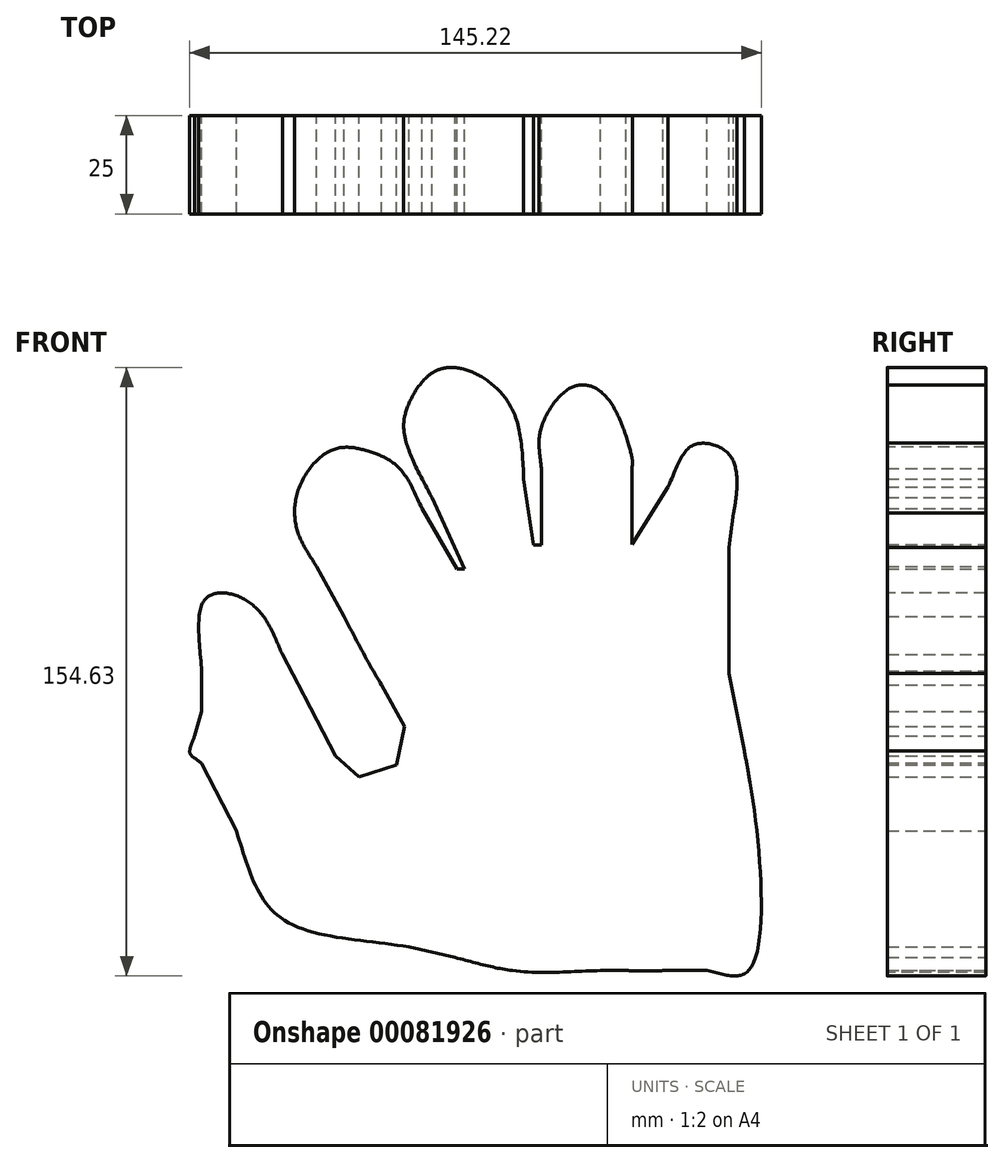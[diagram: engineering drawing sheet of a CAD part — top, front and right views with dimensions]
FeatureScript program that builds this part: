
annotation { "Feature Type Name" : "Feature", "Feature Type Description" : "" }
export const myFeature = defineFeature(function(context is Context, id is Id, definition is map)
    precondition{}
    {
        {
            var Q0;
            Q0=qCreatedBy(makeId("Front.planeOp"),FACE);
            var sketch = newSketch(context, id + "F0", { "sketchPlane" : qUnion([Q0])});
            skLineSegment(sketch, "E0", {"start": v(-6.6, -64.84) * mm, "end": v(53.4, -64.84) * mm});
            skLineSegment(sketch, "E1", {"start": v(53.4, -64.84) * mm, "end": v(53.4, -14.84) * mm});
            skLineSegment(sketch, "E2", {"start": v(53.4, -14.84) * mm, "end": v(48.4, 10.68) * mm});
            skLineSegment(sketch, "E3", {"start": v(48.4, 10.68) * mm, "end": v(48.4, 42.68) * mm});
            skLineSegment(sketch, "E4", {"start": v(48.4, 42.68) * mm, "end": v(50.4, 57.54) * mm});
            skLineSegment(sketch, "E5", {"start": v(50.4, 57.54) * mm, "end": v(48.4, 66.32) * mm});
            skLineSegment(sketch, "E6", {"start": v(48.4, 66.32) * mm, "end": v(39.76, 68.82) * mm});
            skLineSegment(sketch, "E7", {"start": v(39.76, 68.82) * mm, "end": v(23.76, 43.44) * mm});
            skLineSegment(sketch, "E8", {"start": v(23.76, 43.44) * mm, "end": v(23.76, 65.44) * mm});
            skLineSegment(sketch, "E9", {"start": v(23.76, 65.44) * mm, "end": v(20.76, 74.98) * mm});
            skLineSegment(sketch, "E10", {"start": v(20.76, 74.98) * mm, "end": v(14.76, 82.98) * mm});
            skLineSegment(sketch, "E11", {"start": v(14.76, 82.98) * mm, "end": v(7.76, 82.98) * mm});
            skLineSegment(sketch, "E12", {"start": v(7.76, 82.98) * mm, "end": v(0.76, 73.23) * mm});
            skLineSegment(sketch, "E13", {"start": v(0.76, 73.23) * mm, "end": v(0.76, 43.23) * mm});
            skLineSegment(sketch, "E14", {"start": v(0.76, 43.23) * mm, "end": v(-1.24, 43.23) * mm});
            skLineSegment(sketch, "E15", {"start": v(-1.24, 43.23) * mm, "end": v(-6.24, 76.86) * mm});
            skLineSegment(sketch, "E16", {"start": v(-6.24, 76.86) * mm, "end": v(-13.74, 85.58) * mm});
            skLineSegment(sketch, "E17", {"start": v(-28.74, 85.58) * mm, "end": v(-33.74, 76.92) * mm});
            skLineSegment(sketch, "E18", {"start": v(-33.74, 76.92) * mm, "end": v(-33.74, 69.92) * mm});
            skLineSegment(sketch, "E19", {"start": v(-33.74, 69.92) * mm, "end": v(-18.74, 37.2) * mm});
            skLineSegment(sketch, "E20", {"start": v(-18.74, 37.2) * mm, "end": v(-20.74, 37.2) * mm});
            skLineSegment(sketch, "E21", {"start": v(-20.74, 37.2) * mm, "end": v(-35.74, 63.17) * mm});
            skLineSegment(sketch, "E22", {"start": v(-35.74, 63.17) * mm, "end": v(-43.74, 67.3) * mm});
            skLineSegment(sketch, "E23", {"start": v(-43.74, 67.3) * mm, "end": v(-52.74, 67.3) * mm});
            skLineSegment(sketch, "E24", {"start": v(-52.74, 67.3) * mm, "end": v(-61.02, 57.28) * mm});
            skLineSegment(sketch, "E25", {"start": v(-61.02, 57.28) * mm, "end": v(-61.02, 46.28) * mm});
            skLineSegment(sketch, "E26", {"start": v(-61.02, 46.28) * mm, "end": v(-34.02, -2.78) * mm});
            skLineSegment(sketch, "E27", {"start": v(-34.02, -2.78) * mm, "end": v(-36.02, -12.58) * mm});
            skLineSegment(sketch, "E28", {"start": v(-36.02, -12.58) * mm, "end": v(-45.56, -15.58) * mm});
            skLineSegment(sketch, "E29", {"start": v(-45.56, -15.58) * mm, "end": v(-51.56, -10.29) * mm});
            skLineSegment(sketch, "E30", {"start": v(-51.56, -10.29) * mm, "end": v(-70.56, 26.04) * mm});
            skLineSegment(sketch, "E31", {"start": v(-70.56, 26.04) * mm, "end": v(-79.22, 31.04) * mm});
            skLineSegment(sketch, "E32", {"start": v(-79.22, 31.04) * mm, "end": v(-79.22, 28.04) * mm});
            skLineSegment(sketch, "E33", {"start": v(-79.22, 31.04) * mm, "end": v(-85.55, 28.04) * mm});
            skLineSegment(sketch, "E34", {"start": v(-85.55, 28.04) * mm, "end": v(-85.55, 1.04) * mm});
            skLineSegment(sketch, "E35", {"start": v(-85.55, 1.04) * mm, "end": v(-88.55, -9.54) * mm});
            skLineSegment(sketch, "E36", {"start": v(-88.55, -9.54) * mm, "end": v(-85.55, -12.19) * mm});
            skLineSegment(sketch, "E37", {"start": v(-85.55, -12.19) * mm, "end": v(-65.55, -51.38) * mm});
            skLineSegment(sketch, "E38", {"start": v(-65.55, -51.38) * mm, "end": v(-6.6, -64.84) * mm});
            skLineSegment(sketch, "E39", {"start": v(-65.55, -51.38) * mm, "end": v(-44.93, -34.8) * mm});
            skLineSegment(sketch, "E40", {"start": v(-44.93, -34.8) * mm, "end": v(-5.2, -48.3) * mm});
            skLineSegment(sketch, "E41", {"start": v(-5.2, -48.3) * mm, "end": v(-6.6, -64.84) * mm});
            skLineSegment(sketch, "E42", {"start": v(-5.2, -48.3) * mm, "end": v(15.79, -48.3) * mm});
            skLineSegment(sketch, "E43", {"start": v(15.79, -48.3) * mm, "end": v(15.79, -64.84) * mm});
            skLineSegment(sketch, "E44", {"start": v(15.79, -64.84) * mm, "end": v(15.79, -48.3) * mm});
            skLineSegment(sketch, "E45", {"start": v(15.79, -48.3) * mm, "end": v(31.68, -48.3) * mm});
            skLineSegment(sketch, "E46", {"start": v(31.68, -48.3) * mm, "end": v(31.68, -64.84) * mm});
            skLineSegment(sketch, "E47", {"start": v(31.68, -64.84) * mm, "end": v(31.68, -48.3) * mm});
            skLineSegment(sketch, "E48", {"start": v(31.68, -48.3) * mm, "end": v(42.8, -48.3) * mm});
            skLineSegment(sketch, "E49", {"start": v(42.8, -48.3) * mm, "end": v(42.8, -64.84) * mm});
            skLineSegment(sketch, "E50", {"start": v(42.8, -64.84) * mm, "end": v(42.8, -48.3) * mm});
            skLineSegment(sketch, "E51", {"start": v(42.8, -48.3) * mm, "end": v(37.56, -15.08) * mm});
            skLineSegment(sketch, "E52", {"start": v(37.56, -15.08) * mm, "end": v(53.4, -14.84) * mm});
            skLineSegment(sketch, "E53", {"start": v(31.68, -48.3) * mm, "end": v(24.85, -15.88) * mm});
            skLineSegment(sketch, "E54", {"start": v(24.85, -15.88) * mm, "end": v(37.56, -15.08) * mm});
            skLineSegment(sketch, "E55", {"start": v(15.79, -48.3) * mm, "end": v(10.07, -16.51) * mm});
            skLineSegment(sketch, "E56", {"start": v(10.07, -16.51) * mm, "end": v(24.85, -15.88) * mm});
            skLineSegment(sketch, "E57", {"start": v(-5.2, -48.3) * mm, "end": v(-8.7, -16.04) * mm});
            skLineSegment(sketch, "E58", {"start": v(-8.7, -16.04) * mm, "end": v(10.07, -16.51) * mm});
            skLineSegment(sketch, "E59", {"start": v(-36.02, -12.58) * mm, "end": v(-8.7, -16.04) * mm});
            skLineSegment(sketch, "E60", {"start": v(-45.56, -15.58) * mm, "end": v(-44.93, -34.8) * mm});
            skLineSegment(sketch, "E61", {"start": v(-26.95, -40.9) * mm, "end": v(-22.36, -14.3) * mm});
            skLineSegment(sketch, "E62", {"start": v(-22.36, -14.3) * mm, "end": v(-26.95, -40.9) * mm});
            skLineSegment(sketch, "E63", {"start": v(-26.95, -40.9) * mm, "end": v(-32.9, -58.83) * mm});
            skLineSegment(sketch, "E64", {"start": v(-32.9, -58.83) * mm, "end": v(-26.95, -40.9) * mm});
            skLineSegment(sketch, "E65", {"start": v(-76.76, -29.41) * mm, "end": v(-62.41, -20.17) * mm});
            skLineSegment(sketch, "E66", {"start": v(-62.41, -20.17) * mm, "end": v(-44.93, -34.8) * mm});
            skLineSegment(sketch, "E67", {"start": v(-62.41, -20.17) * mm, "end": v(-71, -3.64) * mm});
            skLineSegment(sketch, "E68", {"start": v(-71, -3.64) * mm, "end": v(-51.56, -10.29) * mm});
            skLineSegment(sketch, "E69", {"start": v(-62.41, -20.17) * mm, "end": v(-51.56, -10.29) * mm});
            skLineSegment(sketch, "E70", {"start": v(-85.55, -12.19) * mm, "end": v(-71, -3.64) * mm});
            skLineSegment(sketch, "E71", {"start": v(-71, -3.64) * mm, "end": v(-59.48, 4.84) * mm});
            skLineSegment(sketch, "E72", {"start": v(-59.48, 4.84) * mm, "end": v(-71, -3.64) * mm});
            skLineSegment(sketch, "E73", {"start": v(-71, -3.64) * mm, "end": v(-78.11, 8.47) * mm});
            skLineSegment(sketch, "E74", {"start": v(-78.11, 8.47) * mm, "end": v(-70.56, 26.04) * mm});
            skLineSegment(sketch, "E75", {"start": v(-78.11, 8.47) * mm, "end": v(-85.55, 1.04) * mm});
            skLineSegment(sketch, "E76", {"start": v(-78.11, 8.47) * mm, "end": v(-80.53, 22.59) * mm});
            skLineSegment(sketch, "E77", {"start": v(-80.53, 22.59) * mm, "end": v(-79.22, 31.04) * mm});
            skLineSegment(sketch, "E78", {"start": v(-80.53, 22.59) * mm, "end": v(-85.55, 28.04) * mm});
            skLineSegment(sketch, "E79", {"start": v(-88.55, -9.54) * mm, "end": v(-79.42, -2.2) * mm});
            skLineSegment(sketch, "E80", {"start": v(-79.42, -2.2) * mm, "end": v(-74.55, 2.42) * mm});
            skLineSegment(sketch, "E81", {"start": v(-74.55, 2.42) * mm, "end": v(-65.04, 15.48) * mm});
            skLineSegment(sketch, "E82", {"start": v(-65.04, 15.48) * mm, "end": v(-74.55, 2.42) * mm});
            skLineSegment(sketch, "E83", {"start": v(-22.36, -14.3) * mm, "end": v(-20.74, 37.2) * mm});
            skLineSegment(sketch, "E84", {"start": v(-8.7, -16.04) * mm, "end": v(-18.74, 37.2) * mm});
            skLineSegment(sketch, "E85", {"start": v(10.07, -16.51) * mm, "end": v(-1.24, 43.23) * mm});
            skLineSegment(sketch, "E86", {"start": v(24.85, -15.88) * mm, "end": v(0.76, 43.23) * mm});
            skLineSegment(sketch, "E87", {"start": v(37.56, -15.08) * mm, "end": v(23.76, 43.44) * mm});
            skLineSegment(sketch, "E88", {"start": v(48.4, 10.68) * mm, "end": v(31.49, 10.68) * mm});
            skLineSegment(sketch, "E89", {"start": v(31.49, 10.68) * mm, "end": v(14.03, 10.68) * mm});
            skLineSegment(sketch, "E90", {"start": v(14.03, 10.68) * mm, "end": v(4.92, 10.68) * mm});
            skLineSegment(sketch, "E91", {"start": v(4.92, 10.68) * mm, "end": v(-13.5, 9.39) * mm});
            skLineSegment(sketch, "E92", {"start": v(-13.5, 9.39) * mm, "end": v(-21.61, 9.39) * mm});
            skLineSegment(sketch, "E93", {"start": v(-21.61, 9.39) * mm, "end": v(-39.82, 7.75) * mm});
            skLineSegment(sketch, "E94", {"start": v(-39.82, 7.75) * mm, "end": v(-49.4, 25.15) * mm});
            skLineSegment(sketch, "E95", {"start": v(-49.4, 25.15) * mm, "end": v(-20.74, 37.2) * mm});
            skLineSegment(sketch, "E96", {"start": v(-18.74, 37.2) * mm, "end": v(0, 37.2) * mm});
            skLineSegment(sketch, "E97", {"start": v(0, 37.2) * mm, "end": v(2.76, 38.32) * mm});
            skLineSegment(sketch, "E98", {"start": v(2.76, 38.32) * mm, "end": v(24.97, 38.32) * mm});
            skLineSegment(sketch, "E99", {"start": v(24.97, 38.32) * mm, "end": v(48.4, 36.1) * mm});
            skLineSegment(sketch, "E100", {"start": v(-56.38, 37.83) * mm, "end": v(-29.61, 52.56) * mm});
            skLineSegment(sketch, "E101", {"start": v(-29.61, 52.56) * mm, "end": v(-56.38, 37.83) * mm});
            skLineSegment(sketch, "E102", {"start": v(-27.06, 55.35) * mm, "end": v(-4.05, 62.15) * mm});
            skLineSegment(sketch, "E103", {"start": v(-4.05, 62.15) * mm, "end": v(-27.06, 55.35) * mm});
            skLineSegment(sketch, "E104", {"start": v(0.76, 62.73) * mm, "end": v(23.76, 62.73) * mm});
            skLineSegment(sketch, "E105", {"start": v(23.76, 62.73) * mm, "end": v(0.76, 62.73) * mm});
            skLineSegment(sketch, "E106", {"start": v(32.95, 58.02) * mm, "end": v(49.58, 51.37) * mm});
            skLineSegment(sketch, "E107", {"start": v(49.58, 51.37) * mm, "end": v(32.95, 58.02) * mm});
            skLineSegment(sketch, "E108", {"start": v(-9.37, 37.2) * mm, "end": v(-15.56, 58.75) * mm});
            skLineSegment(sketch, "E109", {"start": v(-15.56, 58.75) * mm, "end": v(-22.46, 88.4) * mm});
            skLineSegment(sketch, "E110", {"start": v(-22.46, 88.4) * mm, "end": v(-19.37, 75.14) * mm});
            skLineSegment(sketch, "E111", {"start": v(-19.37, 75.14) * mm, "end": v(-33.74, 69.92) * mm});
            skLineSegment(sketch, "E112", {"start": v(-19.37, 75.14) * mm, "end": v(-6.24, 76.86) * mm});
            skLineSegment(sketch, "E113", {"start": v(0.76, 73.23) * mm, "end": v(11.33, 73.23) * mm});
            skLineSegment(sketch, "E114", {"start": v(11.33, 73.23) * mm, "end": v(20.76, 74.98) * mm});
            skLineSegment(sketch, "E115", {"start": v(-43, 45.2) * mm, "end": v(-54.2, 65.54) * mm});
            skLineSegment(sketch, "E116", {"start": v(-54.2, 65.54) * mm, "end": v(-48.6, 55.37) * mm});
            skLineSegment(sketch, "E117", {"start": v(-48.6, 55.37) * mm, "end": v(-35.74, 63.17) * mm});
            skLineSegment(sketch, "E118", {"start": v(-61.02, 46.28) * mm, "end": v(-48.6, 55.37) * mm});
            skFitSpline(sketch, "E119", {"points": [v(-85.55, 28.04) * mm, v(-79.22, 31.04) * mm, v(-70.56, 26.04) * mm, v(-65.04, 15.48) * mm, v(-59.48, 4.84) * mm, v(-51.56, -10.29) * mm, v(-45.56, -15.58) * mm, v(-36.02, -12.58) * mm, v(-34.02, -2.78) * mm, v(-39.82, 7.75) * mm, v(-49.4, 25.15) * mm, v(-56.38, 37.83) * mm, v(-61.02, 46.28) * mm, v(-61.02, 57.28) * mm, v(-52.74, 67.3) * mm, v(-43.74, 67.3) * mm, v(-35.74, 63.17) * mm, v(-29.61, 52.56) * mm, v(-20.74, 37.2) * mm, v(-18.74, 37.2) * mm, v(-27.06, 55.35) * mm, v(-33.74, 69.92) * mm, v(-33.74, 76.92) * mm, v(-28.74, 85.58) * mm, v(-22.46, 88.4) * mm, v(-13.74, 85.58) * mm, v(-6.24, 76.86) * mm, v(-3.74, 60.05) * mm, v(-1.24, 43.23) * mm, v(0.76, 43.23) * mm, v(0.76, 62.73) * mm, v(0.76, 73.23) * mm, v(7.76, 82.98) * mm, v(14.76, 82.98) * mm, v(20.76, 74.98) * mm, v(23.76, 65.44) * mm, v(23.76, 62.73) * mm, v(23.76, 43.44) * mm, v(32.95, 58.02) * mm, v(39.76, 68.82) * mm, v(48.4, 66.32) * mm, v(50.4, 57.54) * mm, v(49.58, 51.37) * mm, v(48.4, 42.68) * mm, v(48.4, 36.1) * mm, v(48.4, 10.68) * mm, v(53.4, -14.84) * mm, v(53.4, -64.84) * mm, v(42.8, -64.84) * mm, v(31.68, -64.84) * mm, v(15.79, -64.84) * mm, v(-6.6, -64.84) * mm, v(-32.9, -58.83) * mm, v(-65.55, -51.38) * mm, v(-76.76, -29.41) * mm, v(-85.55, -12.19) * mm, v(-88.55, -9.54) * mm, v(-85.55, 1.04) * mm, v(-85.55, 28.04) * mm]});
            skSolve(sketch);
        }
        {
            var Q0;
            Q0 = qSketchRegion(id + "F0", true);
            var Q1;
            {var subQ0=sQuery(id+"F0.wireOp",EDGE,"E57");Q1=makeQuery(id+"F0.imprint","IMPRINT",FACE,{"disambiguationData":[TD([[makeQuery(id+"F0.imprint","IMPRINT",EDGE,{"derivedFrom":subQ0}),1.0]])]});}
            var Q2;
            {var subQ5=sQuery(id+"F0.wireOp",EDGE,"E92");Q2=makeQuery(id+"F0.imprint","IMPRINT",FACE,{"disambiguationData":[TD([[makeQuery(id+"F0.imprint","IMPRINT",EDGE,{"derivedFrom":subQ5}),1.0]])]});}
            var Q3;
            {var subQ0=sQuery(id+"F0.wireOp",EDGE,"E58");Q3=makeQuery(id+"F0.imprint","IMPRINT",FACE,{"disambiguationData":[TD([[makeQuery(id+"F0.imprint","IMPRINT",EDGE,{"derivedFrom":subQ0}),1.0]])]});}
            var Q4;
            Q4=makeQuery(id+"F0.imprint","IMPRINT",FACE,{"disambiguationData":[TD([[makeQuery(id+"F0.imprint","IMPRINT",EDGE,{"derivedFrom":sQuery(id+"F0.wireOp",EDGE,"E42")}),1.0]])]});
            var Q5;
            Q5=makeQuery(id+"F0.imprint","IMPRINT",FACE,{"disambiguationData":[TD([[makeQuery(id+"F0.imprint","IMPRINT",EDGE,{"derivedFrom":sQuery(id+"F0.wireOp",EDGE,"E45")}),1.0]])]});
            var Q6;
            Q6=makeQuery(id+"F0.imprint","IMPRINT",FACE,{"disambiguationData":[TD([[makeQuery(id+"F0.imprint","IMPRINT",EDGE,{"derivedFrom":sQuery(id+"F0.wireOp",EDGE,"E48")}),1.0]])]});
            var Q7;
            {var subQ0=sQuery(id+"F0.wireOp",EDGE,"E54");Q7=makeQuery(id+"F0.imprint","IMPRINT",FACE,{"disambiguationData":[TD([[makeQuery(id+"F0.imprint","IMPRINT",EDGE,{"derivedFrom":subQ0}),1.0]])]});}
            var Q8;
            {var subQ0=sQuery(id+"F0.wireOp",EDGE,"E56");Q8=makeQuery(id+"F0.imprint","IMPRINT",FACE,{"disambiguationData":[TD([[makeQuery(id+"F0.imprint","IMPRINT",EDGE,{"derivedFrom":subQ0}),1.0]])]});}
            var Q9;
            {var subQ0=sQuery(id+"F0.wireOp",EDGE,"E90");Q9=makeQuery(id+"F0.imprint","IMPRINT",FACE,{"disambiguationData":[TD([[makeQuery(id+"F0.imprint","IMPRINT",EDGE,{"derivedFrom":subQ0}),-1.0]])]});}
            var Q10;
            {var subQ0=sQuery(id+"F0.wireOp",EDGE,"E89");Q10=makeQuery(id+"F0.imprint","IMPRINT",FACE,{"disambiguationData":[TD([[makeQuery(id+"F0.imprint","IMPRINT",EDGE,{"derivedFrom":subQ0}),-1.0]])]});}
            var Q11;
            Q11=makeQuery(id+"F0.imprint","IMPRINT",FACE,{"disambiguationData":[TD([[makeQuery(id+"F0.imprint","IMPRINT",EDGE,{"derivedFrom":sQuery(id+"F0.wireOp",EDGE,"E10")}),1.0]])]});
            extrude(context, id + "F1", {"entities" : qUnion([Q0, Q1, Q2, Q3, Q4, Q5, Q6, Q7, Q8, Q9, Q10, Q11]), "endBound" : BoundingType.SYMMETRIC, "depth" : 25 * mm});
        }
    });
